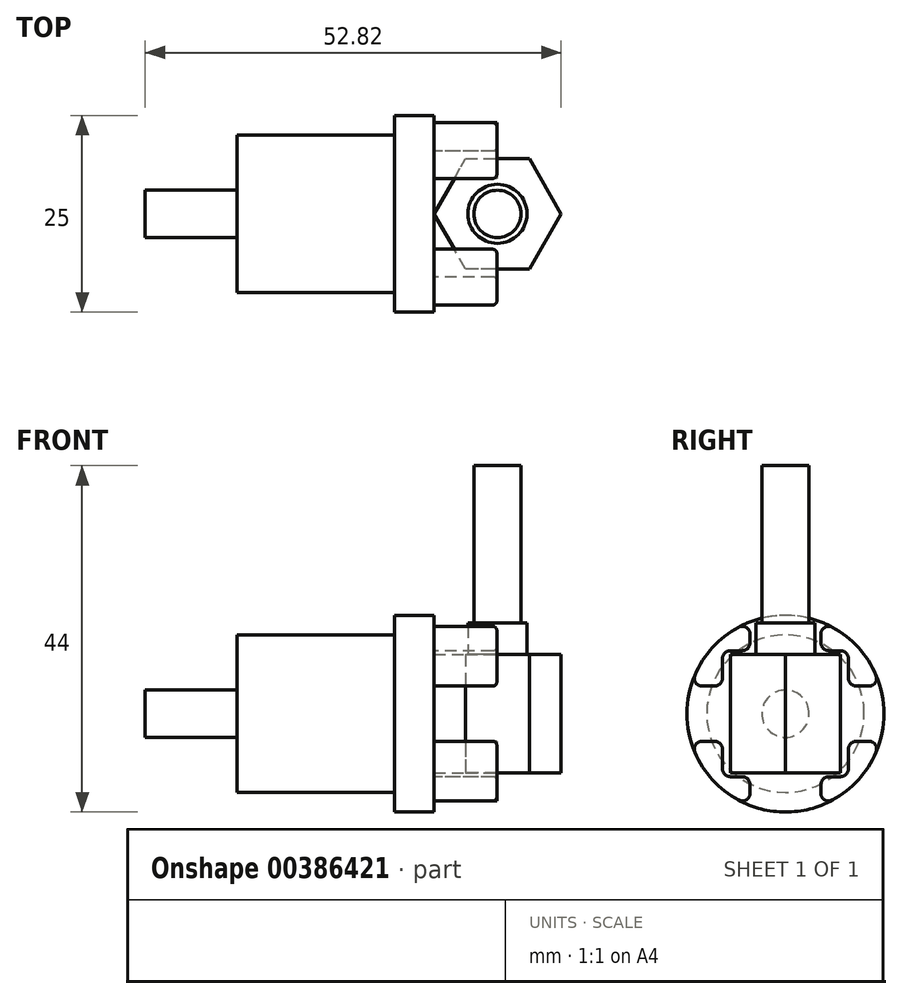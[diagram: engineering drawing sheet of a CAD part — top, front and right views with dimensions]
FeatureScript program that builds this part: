
annotation { "Feature Type Name" : "Feature", "Feature Type Description" : "" }
export const myFeature = defineFeature(function(context is Context, id is Id, definition is map)
    precondition{}
    {
        {
            var Q0;
            Q0=qCreatedBy(makeId("Front.planeOp"),FACE);
            var sketch = newSketch(context, id + "F0", { "sketchPlane" : qUnion([Q0])});
            skLineSegment(sketch, "E0", {"start": v(0, 0) * mm, "end": v(51.78, 0) * mm, "construction": true});
            skLineSegment(sketch, "E1", {"start": v(0, 10) * mm, "end": v(20, 10) * mm});
            skLineSegment(sketch, "E2", {"start": v(20, 10) * mm, "end": v(20, 0) * mm});
            skLineSegment(sketch, "E3", {"start": v(20, 0) * mm, "end": v(0, 0) * mm});
            skLineSegment(sketch, "E4", {"start": v(-11.65, 0) * mm, "end": v(-11.65, 3) * mm});
            skLineSegment(sketch, "E5", {"start": v(-11.65, 3) * mm, "end": v(0, 3) * mm});
            skLineSegment(sketch, "E6", {"start": v(0, 3) * mm, "end": v(0, 10) * mm});
            skLineSegment(sketch, "E7", {"start": v(-11.65, 0) * mm, "end": v(0, 0) * mm});
            skSolve(sketch);
        }
        {
            var Q0;
            Q0 = qSketchRegion(id + "F0", true);
            var Q1;
            Q1=sQuery(id+"F0.wireOp",EDGE,"E0");
            revolve(context, id + "F1", {"entities" : qUnion([Q0]), "axis" : qUnion([Q1]), "revolveType" : RevolveType.FULL});
        }
        {
            var Q0;
            Q0=makeQuery(id+"F1.opRevolve","SWEPT_FACE",FACE,{"disambiguationData":[OSD([sQuery(id+"F0.wireOp",EDGE,"E2")])]});
            var sketch = newSketch(context, id + "F2", { "sketchPlane" : qUnion([Q0])});
            skLineSegment(sketch, "E8", {"start": v(-8.25, 5.65) * mm, "end": v(-8.25, -5.65) * mm});
            skLineSegment(sketch, "E9", {"start": v(0, 0) * mm, "end": v(0, 17.13) * mm, "construction": true});
            skLineSegment(sketch, "E10.MirrorCS", {"start": v(8.25, 5.65) * mm, "end": v(8.25, -5.65) * mm});
            skArc(sketch, "E11.0", {"start": v(-8.25, 5.65) * mm, "mid": v(-10, 0) * mm, "end": v(-8.25, -5.65) * mm});
            skArc(sketch, "E12.trimOffspring", {"start": v(8.25, -5.65) * mm, "mid": v(10, 0) * mm, "end": v(8.25, 5.65) * mm});
            skSolve(sketch);
        }
        {
            var Q0;
            Q0=qCreatedBy(makeId("Top.planeOp"),FACE);
            var sketch = newSketch(context, id + "F3", { "sketchPlane" : qUnion([Q0])});
            skCircle(sketch, "E13.cCircle", {"center": v(33.08, 0) * mm, "radius": 8.08 * mm, "construction": true});
            skLineSegment(sketch, "E13.0", {"start": v(37.12, 7) * mm, "end": v(41.17, 0) * mm});
            skLineSegment(sketch, "E13.1", {"start": v(41.17, 0) * mm, "end": v(37.12, -7) * mm});
            skLineSegment(sketch, "E13.2", {"start": v(37.12, -7) * mm, "end": v(29.04, -7) * mm});
            skLineSegment(sketch, "E13.3", {"start": v(29.04, -7) * mm, "end": v(25, 0) * mm});
            skLineSegment(sketch, "E13.4", {"start": v(25, 0) * mm, "end": v(29.04, 7) * mm});
            skLineSegment(sketch, "E13.5", {"start": v(29.04, 7) * mm, "end": v(37.12, 7) * mm});
            skLineSegment(sketch, "E14", {"start": v(0, 0) * mm, "end": v(49.29, 0) * mm, "construction": true});
            skSolve(sketch);
        }
        {
            var Q0;
            Q0 = qSketchRegion(id + "F3", true);
            extrude(context, id + "F4", {"entities" : qUnion([Q0]), "endBound" : BoundingType.SYMMETRIC, "depth" : 15 * mm});
        }
        {
            var Q0;
            Q0=makeQuery(id+"F1.opRevolve","SWEPT_FACE",FACE,{"disambiguationData":[OSD([sQuery(id+"F0.wireOp",EDGE,"E2")])]});
            var sketch = newSketch(context, id + "F5", { "sketchPlane" : qUnion([Q0])});
            skCircle(sketch, "E15", {"center": v(0, 0) * mm, "radius": 12.5 * mm});
            skSolve(sketch);
        }
        {
            var Q0;
            Q0 = qSketchRegion(id + "F5", true);
            extrude(context, id + "F6", {"entities" : qUnion([Q0]), "depth" : 5 * mm});
        }
        {
            var Q0;
            Q0=makeQuery(id+"F6.opExtrude","CAP_FACE",FACE,{"disambiguationData":[OSD([sQuery(id+"F5.wireOp",EDGE,"E15")])],"isStart":false});
            var sketch = newSketch(context, id + "F7", { "sketchPlane" : qUnion([Q0])});
            skLineSegment(sketch, "E16", {"start": v(0, -17) * mm, "end": v(0, 21.67) * mm, "construction": true});
            skLineSegment(sketch, "E17", {"start": v(-4.5, -9) * mm, "end": v(-4.5, -10.1) * mm});
            skLineSegment(sketch, "E18", {"start": v(-8, -7) * mm, "end": v(-8, -4.5) * mm});
            skArc(sketch, "E19.0", {"start": v(-11.5, -4.9) * mm, "mid": v(-9.26, -8.4) * mm, "end": v(-5.98, -10.98) * mm});
            skArc(sketch, "E20.trimOffspring", {"start": v(5.98, -10.98) * mm, "mid": v(12.44, -1.22) * mm, "end": v(8, 9.6) * mm});
            skPoint(sketch, "E21.visualSharp", {"position": v(-4.5, -11.66) * mm});
            skArc(sketch, "E21.filletArc", {"start": v(-5.98, -10.98) * mm, "mid": v(-4.99, -10.96) * mm, "end": v(-4.5, -10.1) * mm});
            skLineSegment(sketch, "E22", {"start": v(-10.58, -3.5) * mm, "end": v(-9, -3.5) * mm});
            skLineSegment(sketch, "E23", {"start": v(0, 0) * mm, "end": v(-17.48, 0) * mm, "construction": true});
            skPoint(sketch, "E24.newPointB", {"position": v(-8, 9.6) * mm});
            skArc(sketch, "E24.filletArc", {"start": v(-10.58, -3.5) * mm, "mid": v(-11.42, -3.95) * mm, "end": v(-11.5, -4.9) * mm});
            skPoint(sketch, "E25.visualSharp", {"position": v(-8, -3.5) * mm});
            skArc(sketch, "E25.filletArc", {"start": v(-8, -4.5) * mm, "mid": v(-8.3, -3.8) * mm, "end": v(-9, -3.5) * mm});
            skLineSegment(sketch, "E26", {"start": v(-7, -8) * mm, "end": v(-5.5, -8) * mm});
            skPoint(sketch, "E27.visualSharp", {"position": v(-8, -8) * mm});
            skArc(sketch, "E27.filletArc", {"start": v(-8, -7) * mm, "mid": v(-7.7, -7.7) * mm, "end": v(-7, -8) * mm});
            skPoint(sketch, "E28.visualSharp", {"position": v(-4.5, -8) * mm});
            skArc(sketch, "E28.filletArc", {"start": v(-4.5, -9) * mm, "mid": v(-4.8, -8.3) * mm, "end": v(-5.5, -8) * mm});
            skPoint(sketch, "E29.MirrorP", {"position": v(4.5, -11.66) * mm});
            skArc(sketch, "E30.MirrorCS", {"start": v(8, -4.5) * mm, "mid": v(8.3, -3.8) * mm, "end": v(9, -3.5) * mm});
            skArc(sketch, "E31.MirrorCS", {"start": v(5.98, -10.98) * mm, "mid": v(4.99, -10.96) * mm, "end": v(4.5, -10.1) * mm});
            skPoint(sketch, "E32.MirrorP", {"position": v(8, -3.5) * mm});
            skPoint(sketch, "E33.MirrorP", {"position": v(8, -8) * mm});
            skLineSegment(sketch, "E34.MirrorCS", {"start": v(10.58, -3.5) * mm, "end": v(9, -3.5) * mm});
            skArc(sketch, "E35.MirrorCS", {"start": v(4.5, -9) * mm, "mid": v(4.8, -8.3) * mm, "end": v(5.5, -8) * mm});
            skPoint(sketch, "E36.MirrorP", {"position": v(4.5, -8) * mm});
            skArc(sketch, "E37.MirrorCS", {"start": v(8, -7) * mm, "mid": v(7.7, -7.7) * mm, "end": v(7, -8) * mm});
            skLineSegment(sketch, "E38.MirrorCS", {"start": v(7, -8) * mm, "end": v(5.5, -8) * mm});
            skArc(sketch, "E39.MirrorCS", {"start": v(10.58, -3.5) * mm, "mid": v(11.42, -3.95) * mm, "end": v(11.5, -4.9) * mm});
            skArc(sketch, "E40.MirrorCS", {"start": v(11.5, -4.9) * mm, "mid": v(9.26, -8.4) * mm, "end": v(5.98, -10.98) * mm});
            skLineSegment(sketch, "E41.MirrorCS", {"start": v(8, -7) * mm, "end": v(8, -4.5) * mm});
            skLineSegment(sketch, "E42.MirrorCS", {"start": v(4.5, -9) * mm, "end": v(4.5, -10.1) * mm});
            skPoint(sketch, "E43.MirrorP", {"position": v(8, 8) * mm});
            skArc(sketch, "E44.MirrorCS", {"start": v(11.5, 4.9) * mm, "mid": v(9.26, 8.4) * mm, "end": v(5.98, 10.98) * mm});
            skPoint(sketch, "E45.MirrorP", {"position": v(-4.5, 11.66) * mm});
            skArc(sketch, "E46.MirrorCS", {"start": v(8, 7) * mm, "mid": v(7.7, 7.7) * mm, "end": v(7, 8) * mm});
            skPoint(sketch, "E47.MirrorP", {"position": v(4.5, 8) * mm});
            skArc(sketch, "E48.MirrorCS", {"start": v(-10.58, 3.5) * mm, "mid": v(-11.42, 3.95) * mm, "end": v(-11.5, 4.9) * mm});
            skArc(sketch, "E49.MirrorCS", {"start": v(-8, 4.5) * mm, "mid": v(-8.3, 3.8) * mm, "end": v(-9, 3.5) * mm});
            skArc(sketch, "E50.MirrorCS", {"start": v(4.5, 9) * mm, "mid": v(4.8, 8.3) * mm, "end": v(5.5, 8) * mm});
            skArc(sketch, "E51.MirrorCS", {"start": v(-4.5, 9) * mm, "mid": v(-4.8, 8.3) * mm, "end": v(-5.5, 8) * mm});
            skArc(sketch, "E52.MirrorCS", {"start": v(-8, 7) * mm, "mid": v(-7.7, 7.7) * mm, "end": v(-7, 8) * mm});
            skLineSegment(sketch, "E53.MirrorCS", {"start": v(-7, 8) * mm, "end": v(-5.5, 8) * mm});
            skPoint(sketch, "E54.MirrorP", {"position": v(-4.5, 8) * mm});
            skPoint(sketch, "E55.MirrorP", {"position": v(8, 3.5) * mm});
            skArc(sketch, "E56.MirrorCS", {"start": v(10.58, 3.5) * mm, "mid": v(11.42, 3.95) * mm, "end": v(11.5, 4.9) * mm});
            skLineSegment(sketch, "E57.MirrorCS", {"start": v(8, 7) * mm, "end": v(8, 4.5) * mm});
            skLineSegment(sketch, "E58.MirrorCS", {"start": v(-4.5, 9) * mm, "end": v(-4.5, 10.1) * mm});
            skLineSegment(sketch, "E59.MirrorCS", {"start": v(-8, 7) * mm, "end": v(-8, 4.5) * mm});
            skArc(sketch, "E60.MirrorCS", {"start": v(-11.5, 4.9) * mm, "mid": v(-9.26, 8.4) * mm, "end": v(-5.98, 10.98) * mm});
            skPoint(sketch, "E61.MirrorP", {"position": v(-8, 3.5) * mm});
            skPoint(sketch, "E62.MirrorP", {"position": v(-8, 8) * mm});
            skArc(sketch, "E63.MirrorCS", {"start": v(-5.98, 10.98) * mm, "mid": v(-4.99, 10.96) * mm, "end": v(-4.5, 10.1) * mm});
            skLineSegment(sketch, "E64.MirrorCS", {"start": v(7, 8) * mm, "end": v(5.5, 8) * mm});
            skLineSegment(sketch, "E65.MirrorCS", {"start": v(10.58, 3.5) * mm, "end": v(9, 3.5) * mm});
            skLineSegment(sketch, "E66.MirrorCS", {"start": v(4.5, 9) * mm, "end": v(4.5, 10.1) * mm});
            skPoint(sketch, "E67.MirrorP", {"position": v(4.5, 11.66) * mm});
            skArc(sketch, "E68.MirrorCS", {"start": v(8, 4.5) * mm, "mid": v(8.3, 3.8) * mm, "end": v(9, 3.5) * mm});
            skArc(sketch, "E69.MirrorCS", {"start": v(5.98, 10.98) * mm, "mid": v(4.99, 10.96) * mm, "end": v(4.5, 10.1) * mm});
            skLineSegment(sketch, "E70.MirrorCS", {"start": v(-10.58, 3.5) * mm, "end": v(-9, 3.5) * mm});
            skSolve(sketch);
        }
        {
            var Q0;
            Q0 = qSketchRegion(id + "F7", true);
            extrude(context, id + "F8", {"entities" : qUnion([Q0]), "depth" : 8 * mm});
        }
        {
            var Q0;
            Q0=makeQuery(id+"F8.opExtrude","CAP_EDGE",EDGE,{"disambiguationData":[OSD([sQuery(id+"F7.wireOp",EDGE,"E70.MirrorCS")])],"isStart":false});
            var Q1;
            Q1=makeQuery(id+"F8.opExtrude","CAP_EDGE",EDGE,{"disambiguationData":[OSD([sQuery(id+"F7.wireOp",EDGE,"E48.MirrorCS")])],"isStart":false});
            var Q2;
            Q2=makeQuery(id+"F8.opExtrude","CAP_EDGE",EDGE,{"disambiguationData":[OSD([sQuery(id+"F7.wireOp",EDGE,"E60.MirrorCS")])],"isStart":false});
            var Q3;
            Q3=makeQuery(id+"F8.opExtrude","CAP_EDGE",EDGE,{"disambiguationData":[OSD([sQuery(id+"F7.wireOp",EDGE,"E63.MirrorCS")])],"isStart":false});
            var Q4;
            Q4=makeQuery(id+"F8.opExtrude","CAP_EDGE",EDGE,{"disambiguationData":[OSD([sQuery(id+"F7.wireOp",EDGE,"E19.0")])],"isStart":false});
            var Q5;
            Q5=makeQuery(id+"F8.opExtrude","CAP_EDGE",EDGE,{"disambiguationData":[OSD([sQuery(id+"F7.wireOp",EDGE,"E40.MirrorCS")])],"isStart":false});
            var Q6;
            Q6=makeQuery(id+"F8.opExtrude","CAP_EDGE",EDGE,{"disambiguationData":[OSD([sQuery(id+"F7.wireOp",EDGE,"E44.MirrorCS")])],"isStart":false});
            fillet(context, id + "F9", {"entities" : qUnion([Q0, Q1, Q2, Q3, Q4, Q5, Q6]), "radius" : 0.5 * mm, "tangentPropagation" : true, "allowEdgeOverflow" : false});
        }
        {
            var Q0;
            Q0=makeQuery(id+"F4.opExtrude","CAP_FACE",FACE,{"disambiguationData":[OSD([sQuery(id+"F3.wireOp",EDGE,"E13.0"),sQuery(id+"F3.wireOp",EDGE,"E13.1"),sQuery(id+"F3.wireOp",EDGE,"E13.2"),sQuery(id+"F3.wireOp",EDGE,"E13.3"),sQuery(id+"F3.wireOp",EDGE,"E13.4"),sQuery(id+"F3.wireOp",EDGE,"E13.5")])],"isStart":false});
            var sketch = newSketch(context, id + "F10", { "sketchPlane" : qUnion([Q0])});
            skCircle(sketch, "E71", {"center": v(33.08, 0) * mm, "radius": 3.75 * mm});
            skSolve(sketch);
        }
        {
            var Q0;
            Q0 = qSketchRegion(id + "F10", true);
            extrude(context, id + "F11", {"entities" : qUnion([Q0]), "operationType" : NewBodyOperationType.ADD, "depth" : 4 * mm});
        }
        {
            var Q0;
            Q0=makeQuery(id+"F11.opExtrude","CAP_FACE",FACE,{"disambiguationData":[OSD([sQuery(id+"F10.wireOp",EDGE,"E71")])],"isStart":false});
            var sketch = newSketch(context, id + "F12", { "sketchPlane" : qUnion([Q0])});
            skCircle(sketch, "E72", {"center": v(33.08, 0) * mm, "radius": 3 * mm});
            skSolve(sketch);
        }
        {
            var Q0;
            Q0 = qSketchRegion(id + "F12", true);
            extrude(context, id + "F13", {"entities" : qUnion([Q0]), "operationType" : NewBodyOperationType.ADD, "depth" : 20 * mm});
        }
    });
